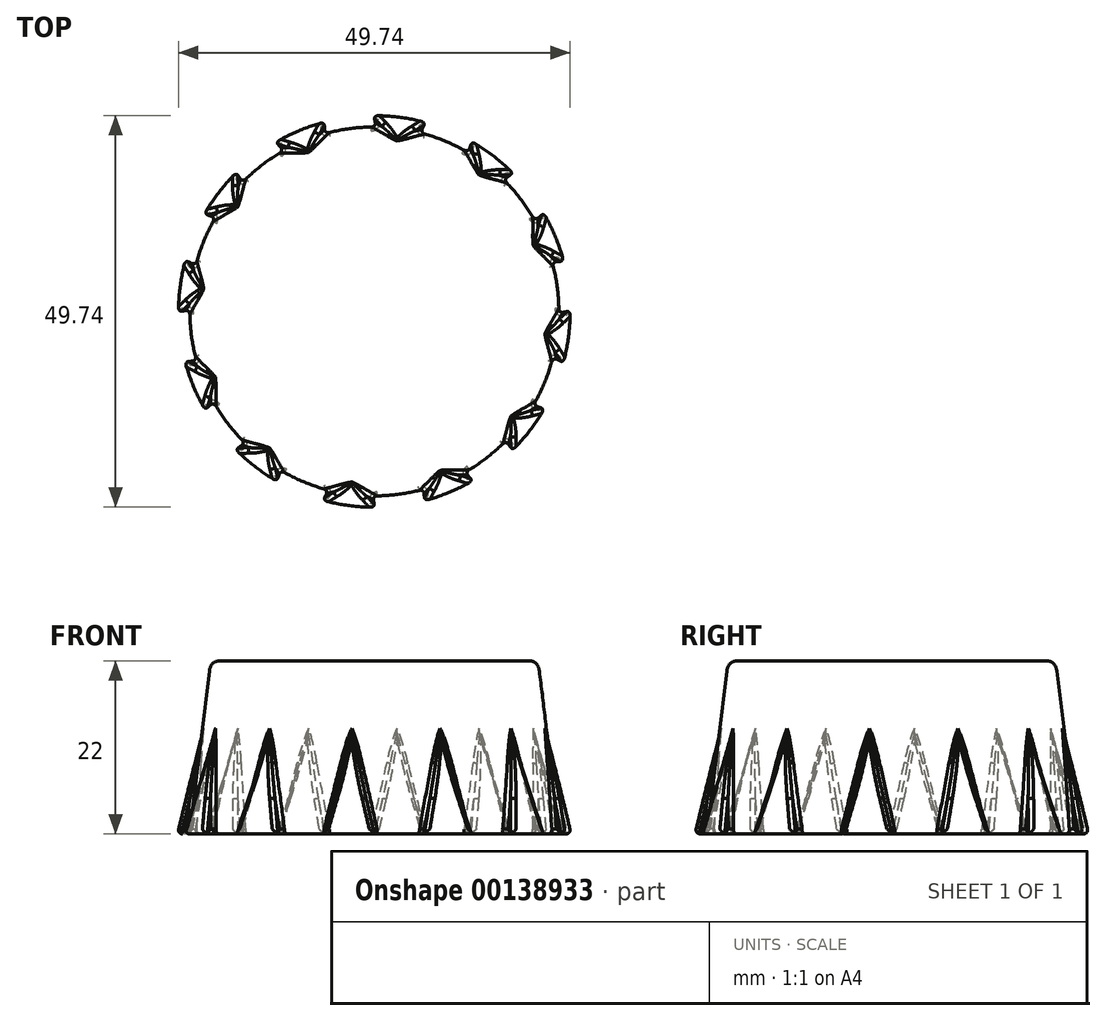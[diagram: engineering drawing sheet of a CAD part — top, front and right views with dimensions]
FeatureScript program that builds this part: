
annotation { "Feature Type Name" : "Feature", "Feature Type Description" : "" }
export const myFeature = defineFeature(function(context is Context, id is Id, definition is map)
    precondition{}
    {
        {
            var Q0;
            Q0=qCreatedBy(makeId("Top.planeOp"),FACE);
            var sketch = newSketch(context, id + "F0", { "sketchPlane" : qUnion([Q0])});
            skCircle(sketch, "E0", {"center": v(0, 0) * mm, "radius": 23.5 * mm});
            skSolve(sketch);
        }
        {
            var Q0;
            Q0=makeQuery(id+"F0.imprint","IMPRINT",FACE,{"disambiguationData":[TD([[makeQuery(id+"F0.imprint","IMPRINT",EDGE,{"derivedFrom":sQuery(id+"F0.wireOp",EDGE,"E0")}),1.0]])]});
            extrude(context, id + "F1", {"entities" : qUnion([Q0]), "depth" : 22 * mm, "hasDraft" : true, "draftAngle" : 7 * degree, "draftPullDirection" : true});
        }
        {
            var Q0;
            Q0=qCreatedBy(makeId("Top.planeOp"),FACE);
            var sketch = newSketch(context, id + "F2", { "sketchPlane" : qUnion([Q0])});
            skCircle(sketch, "E1", {"center": v(0, 0) * mm, "radius": 25 * mm, "construction": true});
            skLineSegment(sketch, "E2", {"start": v(0, 0) * mm, "end": v(0, 25) * mm, "construction": true});
            skLineSegment(sketch, "E3", {"start": v(0, 0) * mm, "end": v(12.5, 21.65) * mm, "construction": true});
            skArc(sketch, "E4", {"start": v(6.47, 24.15) * mm, "mid": v(3.26, 24.79) * mm, "end": v(0, 25) * mm});
            skLineSegment(sketch, "E5", {"start": v(6.47, 24.15) * mm, "end": v(0, 0) * mm, "construction": true});
            skLineSegment(sketch, "E6", {"start": v(6.47, 24.15) * mm, "end": v(6.08, 22.7) * mm});
            skPoint(sketch, "E7", {"position": v(11.75, 20.35) * mm});
            skArc(sketch, "E8", {"start": v(11.75, 20.35) * mm, "mid": v(9, 21.71) * mm, "end": v(6.08, 22.7) * mm});
            skLineSegment(sketch, "E9", {"start": v(11.75, 20.35) * mm, "end": v(12.5, 21.65) * mm});
            skArc(sketch, "E10.1.0", {"start": v(-24.15, -6.47) * mm, "mid": v(-23.1, -9.57) * mm, "end": v(-21.65, -12.5) * mm});
            skLineSegment(sketch, "E10.1.1", {"start": v(-24.15, -6.47) * mm, "end": v(-22.7, -6.08) * mm});
            skArc(sketch, "E10.1.2", {"start": v(-23.5, 0) * mm, "mid": v(-23.3, -3.07) * mm, "end": v(-22.7, -6.08) * mm});
            skLineSegment(sketch, "E10.1.3", {"start": v(-23.5, 0) * mm, "end": v(-25, 0) * mm});
            skArc(sketch, "E10.2.0", {"start": v(17.68, -17.68) * mm, "mid": v(19.83, -15.22) * mm, "end": v(21.65, -12.5) * mm});
            skLineSegment(sketch, "E10.2.1", {"start": v(17.68, -17.68) * mm, "end": v(16.62, -16.62) * mm});
            skArc(sketch, "E10.2.2", {"start": v(11.75, -20.35) * mm, "mid": v(14.3, -18.64) * mm, "end": v(16.62, -16.62) * mm});
            skLineSegment(sketch, "E10.2.3", {"start": v(11.75, -20.35) * mm, "end": v(12.5, -21.65) * mm});
            skArc(sketch, "E11.1.0", {"start": v(-6.47, 24.15) * mm, "mid": v(-9.57, 23.1) * mm, "end": v(-12.5, 21.65) * mm});
            skLineSegment(sketch, "E11.1.1", {"start": v(-6.47, 24.15) * mm, "end": v(-6.08, 22.7) * mm});
            skArc(sketch, "E11.1.2", {"start": v(0, 23.5) * mm, "mid": v(-3.07, 23.3) * mm, "end": v(-6.08, 22.7) * mm});
            skLineSegment(sketch, "E11.1.3", {"start": v(0, 23.5) * mm, "end": v(0, 25) * mm});
            skArc(sketch, "E11.2.0", {"start": v(-17.68, 17.68) * mm, "mid": v(-19.83, 15.22) * mm, "end": v(-21.65, 12.5) * mm});
            skLineSegment(sketch, "E11.2.1", {"start": v(-17.68, 17.68) * mm, "end": v(-16.62, 16.62) * mm});
            skArc(sketch, "E11.2.2", {"start": v(-11.75, 20.35) * mm, "mid": v(-14.3, 18.64) * mm, "end": v(-16.62, 16.62) * mm});
            skLineSegment(sketch, "E11.2.3", {"start": v(-11.75, 20.35) * mm, "end": v(-12.5, 21.65) * mm});
            skArc(sketch, "E11.3.0", {"start": v(-24.15, 6.47) * mm, "mid": v(-24.79, 3.26) * mm, "end": v(-25, 0) * mm});
            skLineSegment(sketch, "E11.3.1", {"start": v(-24.15, 6.47) * mm, "end": v(-22.7, 6.08) * mm});
            skArc(sketch, "E11.3.2", {"start": v(-20.35, 11.75) * mm, "mid": v(-21.71, 9) * mm, "end": v(-22.7, 6.08) * mm});
            skLineSegment(sketch, "E11.3.3", {"start": v(-20.35, 11.75) * mm, "end": v(-21.65, 12.5) * mm});
            skArc(sketch, "E11.5.0", {"start": v(-17.68, -17.68) * mm, "mid": v(-15.22, -19.83) * mm, "end": v(-12.5, -21.65) * mm});
            skLineSegment(sketch, "E11.5.1", {"start": v(-17.68, -17.68) * mm, "end": v(-16.62, -16.62) * mm});
            skArc(sketch, "E11.5.2", {"start": v(-20.35, -11.75) * mm, "mid": v(-18.64, -14.3) * mm, "end": v(-16.62, -16.62) * mm});
            skLineSegment(sketch, "E11.5.3", {"start": v(-20.35, -11.75) * mm, "end": v(-21.65, -12.5) * mm});
            skArc(sketch, "E11.6.0", {"start": v(-6.47, -24.15) * mm, "mid": v(-3.26, -24.79) * mm, "end": v(0, -25) * mm});
            skLineSegment(sketch, "E11.6.1", {"start": v(-6.47, -24.15) * mm, "end": v(-6.08, -22.7) * mm});
            skArc(sketch, "E11.6.2", {"start": v(-11.75, -20.35) * mm, "mid": v(-9, -21.71) * mm, "end": v(-6.08, -22.7) * mm});
            skLineSegment(sketch, "E11.6.3", {"start": v(-11.75, -20.35) * mm, "end": v(-12.5, -21.65) * mm});
            skArc(sketch, "E11.7.0", {"start": v(6.47, -24.15) * mm, "mid": v(9.57, -23.1) * mm, "end": v(12.5, -21.65) * mm});
            skLineSegment(sketch, "E11.7.1", {"start": v(6.47, -24.15) * mm, "end": v(6.08, -22.7) * mm});
            skArc(sketch, "E11.7.2", {"start": v(0, -23.5) * mm, "mid": v(3.07, -23.3) * mm, "end": v(6.08, -22.7) * mm});
            skLineSegment(sketch, "E11.7.3", {"start": v(0, -23.5) * mm, "end": v(0, -25) * mm});
            skArc(sketch, "E11.9.0", {"start": v(24.15, -6.47) * mm, "mid": v(24.79, -3.26) * mm, "end": v(25, 0) * mm});
            skLineSegment(sketch, "E11.9.1", {"start": v(24.15, -6.47) * mm, "end": v(22.7, -6.08) * mm});
            skArc(sketch, "E11.9.2", {"start": v(20.35, -11.75) * mm, "mid": v(21.71, -9) * mm, "end": v(22.7, -6.08) * mm});
            skLineSegment(sketch, "E11.9.3", {"start": v(20.35, -11.75) * mm, "end": v(21.65, -12.5) * mm});
            skArc(sketch, "E11.10.0", {"start": v(24.15, 6.47) * mm, "mid": v(23.1, 9.57) * mm, "end": v(21.65, 12.5) * mm});
            skLineSegment(sketch, "E11.10.1", {"start": v(24.15, 6.47) * mm, "end": v(22.7, 6.08) * mm});
            skArc(sketch, "E11.10.2", {"start": v(23.5, 0) * mm, "mid": v(23.3, 3.07) * mm, "end": v(22.7, 6.08) * mm});
            skLineSegment(sketch, "E11.10.3", {"start": v(23.5, 0) * mm, "end": v(25, 0) * mm});
            skArc(sketch, "E11.11.0", {"start": v(17.68, 17.68) * mm, "mid": v(15.22, 19.83) * mm, "end": v(12.5, 21.65) * mm});
            skLineSegment(sketch, "E11.11.1", {"start": v(17.68, 17.68) * mm, "end": v(16.62, 16.62) * mm});
            skArc(sketch, "E11.11.2", {"start": v(20.35, 11.75) * mm, "mid": v(18.64, 14.3) * mm, "end": v(16.62, 16.62) * mm});
            skLineSegment(sketch, "E11.11.3", {"start": v(20.35, 11.75) * mm, "end": v(21.65, 12.5) * mm});
            skSolve(sketch);
        }
        {
            var Q0;
            Q0 = qSketchRegion(id + "F2", true);
            extrude(context, id + "F3", {"entities" : qUnion([Q0]), "operationType" : NewBodyOperationType.ADD, "depth" : 21 * mm, "hasDraft" : true, "draftAngle" : 13 * degree, "draftPullDirection" : true});
        }
        {
            var Q0;
            Q0=makeQuery(id+"F1.opExtrude","CAP_FACE",FACE,{"disambiguationData":[OSD([sQuery(id+"F0.wireOp",EDGE,"E0")])],"isStart":false});
            fillet(context, id + "F4", {"entities" : qUnion([Q0]), "radius" : 1.5 * mm, "tangentPropagation" : true, "rho" : 0.5, "crossSection" : FilletCrossSection.CONIC, "allowEdgeOverflow" : false});
        }
        {
            var Q0;
            Q0=makeQuery(id+"F1.opExtrude","SWEPT_FACE",FACE,{"disambiguationData":[OSD([sQuery(id+"F0.wireOp",EDGE,"E0")])]});
            fillet(context, id + "F5", {"entities" : qUnion([Q0]), "radius" : .5 * mm, "tangentPropagation" : true, "allowEdgeOverflow" : false});
        }
        {
            var Q0;
            Q0=makeQuery(id+"F3.opExtrude","SWEPT_FACE",FACE,{"disambiguationData":[OSD([sQuery(id+"F2.wireOp",EDGE,"E4")])]});
            var Q1;
            Q1=makeQuery(id+"F3.opExtrude","SWEPT_FACE",FACE,{"disambiguationData":[OSD([sQuery(id+"F2.wireOp",EDGE,"E11.11.0")])]});
            var Q2;
            Q2=makeQuery(id+"F3.opExtrude","SWEPT_FACE",FACE,{"disambiguationData":[OSD([sQuery(id+"F2.wireOp",EDGE,"E11.10.0")])]});
            var Q3;
            Q3=makeQuery(id+"F3.opExtrude","SWEPT_FACE",FACE,{"disambiguationData":[OSD([sQuery(id+"F2.wireOp",EDGE,"E11.9.0")])]});
            var Q4;
            Q4=makeQuery(id+"F3.opExtrude","SWEPT_FACE",FACE,{"disambiguationData":[OSD([sQuery(id+"F2.wireOp",EDGE,"E10.2.0")])]});
            var Q5;
            Q5=makeQuery(id+"F3.opExtrude","SWEPT_FACE",FACE,{"disambiguationData":[OSD([sQuery(id+"F2.wireOp",EDGE,"E11.7.0")])]});
            var Q6;
            Q6=makeQuery(id+"F3.opExtrude","SWEPT_FACE",FACE,{"disambiguationData":[OSD([sQuery(id+"F2.wireOp",EDGE,"E11.6.0")])]});
            var Q7;
            Q7=makeQuery(id+"F3.opExtrude","SWEPT_FACE",FACE,{"disambiguationData":[OSD([sQuery(id+"F2.wireOp",EDGE,"E11.5.0")])]});
            var Q8;
            Q8=makeQuery(id+"F3.opExtrude","SWEPT_FACE",FACE,{"disambiguationData":[OSD([sQuery(id+"F2.wireOp",EDGE,"E10.1.0")])]});
            var Q9;
            Q9=makeQuery(id+"F3.opExtrude","SWEPT_FACE",FACE,{"disambiguationData":[OSD([sQuery(id+"F2.wireOp",EDGE,"E11.3.0")])]});
            var Q10;
            Q10=makeQuery(id+"F3.opExtrude","SWEPT_FACE",FACE,{"disambiguationData":[OSD([sQuery(id+"F2.wireOp",EDGE,"E11.2.0")])]});
            var Q11;
            Q11=makeQuery(id+"F3.opExtrude","SWEPT_FACE",FACE,{"disambiguationData":[OSD([sQuery(id+"F2.wireOp",EDGE,"E11.1.0")])]});
            fillet(context, id + "F6", {"entities" : qUnion([Q0, Q1, Q2, Q3, Q4, Q5, Q6, Q7, Q8, Q9, Q10, Q11]), "radius" : .5 * mm, "tangentPropagation" : true, "allowEdgeOverflow" : false});
        }
    });
